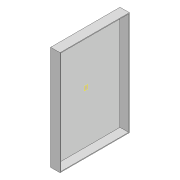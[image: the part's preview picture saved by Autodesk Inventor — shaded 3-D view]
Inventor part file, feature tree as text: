
AUTODESK INVENTOR PART (.ipt)
format: ipt  version: 2022 (Build 260153000, 153)  size: 98,304 bytes
history: native  units: mm
features: other x2, extrude x2, sketch x2
ambient origin geometry x8: Origin, YZ Plane, XZ Plane, XY Plane, X Axis, Y Axis, Z Axis, Center Point
bodies: Body1 (feature_tree)
feature tree (6):
  other  "Твердое тело1"
  other  "РабПлоскость1"
  extrude  "Выдавливание2"  Depth=4.0mm
  extrude  "Выдавливание3"  Depth=4.0mm
  sketch  "Эскиз2"
  sketch  "Эскиз3"
